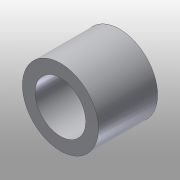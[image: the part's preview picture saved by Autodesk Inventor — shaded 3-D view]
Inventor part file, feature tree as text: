
AUTODESK INVENTOR PART (.ipt)
format: ipt  version: 2016 (Build 200138000, 138)  size: 89,088 bytes
history: native  units: mm
features: extrude x1, sketch x1
ambient origin geometry x8: Origin, YZ Plane, XZ Plane, XY Plane, X Axis, Y Axis, Z Axis, Center Point
bodies: Solid1 (feature_tree)
feature tree (2):
  extrude  "Extrusion1"  Depth=3.5mm
  sketch  "Sketch1"  dims[d0=4.5mm d1=3.0mm d2=3.5mm d3=0.0mm]
